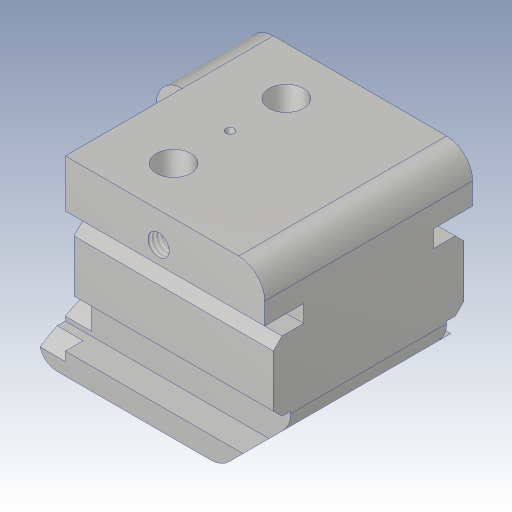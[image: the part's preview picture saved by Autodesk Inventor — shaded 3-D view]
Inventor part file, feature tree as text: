
AUTODESK INVENTOR PART (.ipt)
format: ipt  version: 2023.3 (Build 273359000, 359)  size: 557,056 bytes
history: native  units: in
note: dims shown in document units (in); Inventor stores cm internally (conversion verified against a paired STEP export)
features: sketch x9, hole x7, extrude x4, fillet x2, mirror x1, projected_geometry x1
ambient origin geometry x8: Origin, YZ Plane, XZ Plane, XY Plane, X Axis, Y Axis, Z Axis, Center Point
bodies: Body1 (feature_tree)
feature tree (24):
  extrude  "Extrusion7"  Depth=1.0236in
  sketch  "Skizze25"  dims[d206=0.0937in d207=0.2362in d208=0.1575in d209=0.0787in d210=90.0deg d211=0.1969in d212=0.0in]
  hole  "Bohrung19"  [1 undecoded]
  fillet  "Rundung3"  Radius=0.4724in
  sketch  "Skizze23"  dims[d125=0.9449in d126=0.0in d203=0.1181in d204=0.4724in]
  hole  "Bohrung16"  [1 undecoded]
  hole  "Bohrung18"  [1 undecoded]
  extrude  "Extrusion10"  Depth=0.315in
  hole  "Bohrung22"  [1 undecoded]
  hole  "Bohrung28"  [1 undecoded]
  fillet  "Rundung14"  Radius=0.0394in
  sketch  "Skizze31"  dims[d226=0.0787in d227=0.2756in d228=0.1575in d229=0.5118in d230=90.0deg d231=0.315in d232=0.8108in d233=0.3937in]
  sketch  "Skizze34"  dims[d234=0.0394in d235=0.2362in d236=0.1575in d237=0.0787in d238=90.0deg d239=0.2756in d240=0.0in d248=0.3937in]
  hole  "Bohrung27"  [1 undecoded]
  hole  "Bohrung26"  [1 undecoded]
  extrude  "Extrusion12"  Depth=0.2559in
  mirror  "Spiegeln1"
  extrude  "Extrusion13"  Depth=0.374in
  sketch  "Skizze14"  dims[d122=0.8661in d123=1.0236in]
  sketch  "Skizze24"  dims[d205=0.5118in]
  projected_geometry  "Projizierte Kontur6"
  sketch  "Skizze36"  dims[d321=0.0394in d322=0.0394in d323=0.0394in d324=0.0394in d325=0.0394in]
  sketch  "Skizze37"  dims[d328=0.0394in d329=0.0394in d330=0.0394in d331=0.0394in d332=0.0394in]
  sketch  "Skizze38"  dims[d335=0.0394in d336=0.0394in d337=0.0394in d338=0.0394in d339=0.0394in d342=0.0394in d343=0.0394in d344=0.0394in d345=0.0394in d346=0.0394in d384=0.315in d386=0.3937in d387=0.6496in d388=0.0in d389=0.0394in d425=0.0787in d426=0.5118in d427=0.2559in d428=0.374in d429=0.1772in d431=0.2461in d432=0.1181in d433=0.2362in d434=0.1575in d435=0.5118in d436=90.0deg d437=0.315in d438=0.0in d482=0.0787in d484=0.1378in d485=0.5118in d493=0.0512in d494=0.0512in d495=0.0512in d496=0.0512in d498=0.0787in d499=0.0984in d500=0.0394in d502=0.0394in d509=0.1181in d513=0.3937in d514=0.0in d528=0.374in d529=0.187in d530=0.1181in d531=0.315in d533=0.1855in d534=0.5118in d535=0.1181in d536=0.1181in d537=0.1575in d538=0.1575in d539=0.1181in d540=0.0in d541=0.1855in d542=0.1181in d543=0.3937in d544=0.0394in d545=0.2559in d546=0.0968in d547=0.2362in d548=0.248in d549=0.0787in d550=90.0deg d551=0.3465in d552=0.0in d553=0.0968in d554=0.2362in d555=0.1575in d556=0.0787in d557=90.0deg d558=0.3465in d559=0.0in d560=0.5413in d562=45.0deg d563=0.1969in d564=0.1181in d565=0.1575in d566=0.0787in d567=0.0787in d568=0.0512in d569=0.0512in d570=0.0512in d571=0.0512in d573=0.1181in d574=0.1575in d575=0.1575in d576=0.1181in d577=0.2362in d578=0.1575in d579=0.5118in d580=90.0deg d581=0.315in d582=0.0in d583=0.1575in d584=0.2756in d585=45.0deg d586=0.1772in d587=45.0deg d588=0.0394in d394=0.0197in d395=0.0344in d396=0.0197in d397=0.0344in d404=0.0197in d405=0.0344in d406=0.0197in d407=0.0344in d561=0.0in d572=0.0098in]
note: 7 required parameter values undecoded (feature->parameter linkage not recoverable at this tier; creation-order binding heuristic only, values carry confidence <= 0.55)
